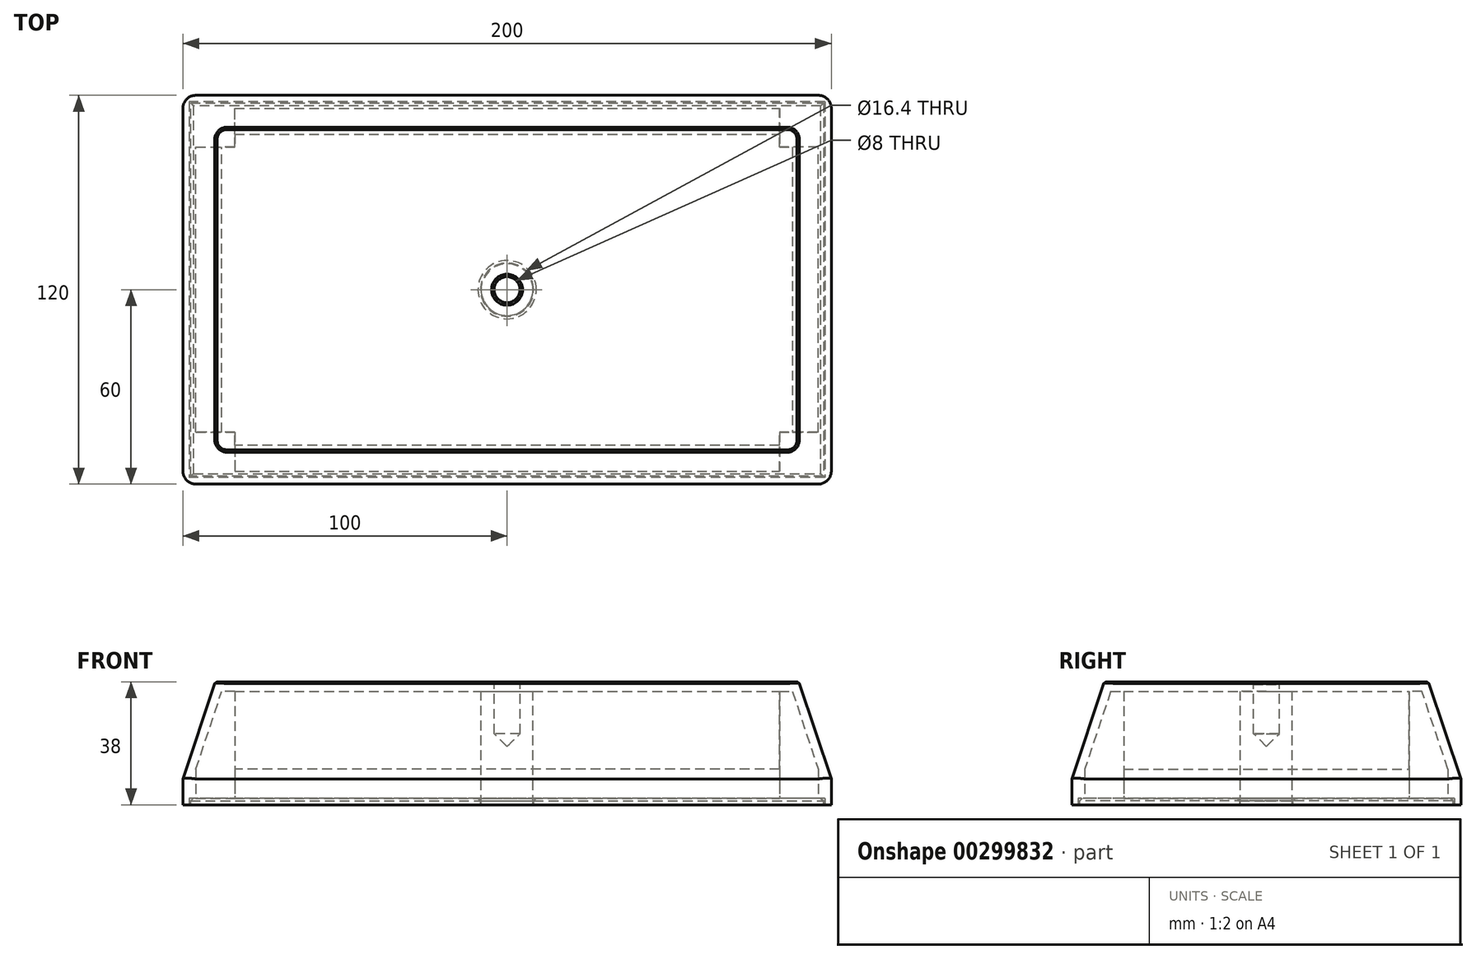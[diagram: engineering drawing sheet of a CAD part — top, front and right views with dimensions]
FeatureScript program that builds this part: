
annotation { "Feature Type Name" : "Feature", "Feature Type Description" : "" }
export const myFeature = defineFeature(function(context is Context, id is Id, definition is map)
    precondition{}
    {
        {
            var Q0;
            Q0=qCreatedBy(makeId("Top.planeOp"),FACE);
            var sketch = newSketch(context, id + "F0", { "sketchPlane" : qUnion([Q0])});
            skLineSegment(sketch, "E0.bottom", {"start": v(100, -60) * mm, "end": v(-100, -60) * mm});
            skLineSegment(sketch, "E0.top", {"start": v(100, 60) * mm, "end": v(-100, 60) * mm});
            skLineSegment(sketch, "E0.left", {"start": v(100, -60) * mm, "end": v(100, 60) * mm});
            skLineSegment(sketch, "E0.right", {"start": v(-100, -60) * mm, "end": v(-100, 60) * mm});
            skPoint(sketch, "E0.middle", {"position": v(0, 0) * mm});
            skSolve(sketch);
        }
        {
            var Q0;
            Q0 = qSketchRegion(id + "F0", true);
            extrude(context, id + "F1", {"entities" : qUnion([Q0]), "depth" : 38 * mm, "offsetDistance" : 25 * mm});
        }
        {
            var Q0;
            Q0=makeQuery(id+"F1.opExtrude","CAP_FACE",FACE,{"disambiguationData":[OSD([sQuery(id+"F0.wireOp",EDGE,"E0.bottom"),sQuery(id+"F0.wireOp",EDGE,"E0.top"),sQuery(id+"F0.wireOp",EDGE,"E0.left"),sQuery(id+"F0.wireOp",EDGE,"E0.right")])],"isStart":true});
            var sketch = newSketch(context, id + "F2", { "sketchPlane" : qUnion([Q0])});
            skLineSegment(sketch, "E1.bottom", {"start": v(84, -56) * mm, "end": v(-84, -56) * mm});
            skLineSegment(sketch, "E1.top", {"start": v(84, 56) * mm, "end": v(-84, 56) * mm});
            skLineSegment(sketch, "E1.left", {"start": v(96, -44) * mm, "end": v(96, 44) * mm});
            skLineSegment(sketch, "E1.right", {"start": v(-96, -44) * mm, "end": v(-96, 44) * mm});
            skPoint(sketch, "E1.middle", {"position": v(0, 0) * mm});
            skLineSegment(sketch, "E2", {"start": v(84, 56) * mm, "end": v(84, 44) * mm});
            skLineSegment(sketch, "E3", {"start": v(84, 44) * mm, "end": v(96, 44) * mm});
            skLineSegment(sketch, "E4.MirrorCS", {"start": v(-84, 56) * mm, "end": v(-84, 44) * mm});
            skLineSegment(sketch, "E5.MirrorCS", {"start": v(-84, 44) * mm, "end": v(-96, 44) * mm});
            skLineSegment(sketch, "E6.MirrorCS", {"start": v(84, -44) * mm, "end": v(96, -44) * mm});
            skLineSegment(sketch, "E7.MirrorCS", {"start": v(84, -56) * mm, "end": v(84, -44) * mm});
            skLineSegment(sketch, "E8.MirrorCS", {"start": v(-84, -56) * mm, "end": v(-84, -44) * mm});
            skLineSegment(sketch, "E9.MirrorCS", {"start": v(-84, -44) * mm, "end": v(-96, -44) * mm});
            skPoint(sketch, "E10.orphan", {"position": v(96, 56) * mm});
            skPoint(sketch, "E11.orphan", {"position": v(96, -56) * mm});
            skPoint(sketch, "E12.orphan", {"position": v(-96, -56) * mm});
            skPoint(sketch, "E13.orphan", {"position": v(-96, 56) * mm});
            skSolve(sketch);
        }
        {
            var Q0;
            Q0 = qSketchRegion(id + "F2", true);
            extrude(context, id + "F3", {"entities" : qUnion([Q0]), "operationType" : NewBodyOperationType.REMOVE, "oppositeDirection" : true, "depth" : 35 * mm, "offsetDistance" : 25 * mm});
        }
        {
            var Q0;
            Q0=makeQuery(id+"F1.opExtrude","CAP_FACE",FACE,{"disambiguationData":[OSD([sQuery(id+"F0.wireOp",EDGE,"E0.bottom"),sQuery(id+"F0.wireOp",EDGE,"E0.top"),sQuery(id+"F0.wireOp",EDGE,"E0.left"),sQuery(id+"F0.wireOp",EDGE,"E0.right")])],"isStart":true});
            var sketch = newSketch(context, id + "F4", { "sketchPlane" : qUnion([Q0])});
            skLineSegment(sketch, "E14.bottom", {"start": v(98, -58) * mm, "end": v(-98, -58) * mm});
            skLineSegment(sketch, "E14.top", {"start": v(98, 58) * mm, "end": v(-98, 58) * mm});
            skLineSegment(sketch, "E14.left", {"start": v(98, -58) * mm, "end": v(98, 58) * mm});
            skLineSegment(sketch, "E14.right", {"start": v(-98, -58) * mm, "end": v(-98, 58) * mm});
            skPoint(sketch, "E14.middle", {"position": v(0, 0) * mm});
            skSolve(sketch);
        }
        {
            var Q0;
            Q0 = qSketchRegion(id + "F4", true);
            extrude(context, id + "F5", {"entities" : qUnion([Q0]), "operationType" : NewBodyOperationType.REMOVE, "oppositeDirection" : true, "depth" : 2 * mm, "offsetDistance" : 25 * mm});
        }
        {
            var Q0;
            Q0=makeQuery(id+"F3.boolean.opBoolean","COPY",FACE,{"derivedFrom":makeQuery(id+"F3.opExtrude","CAP_FACE",FACE,{"disambiguationData":[OSD([sQuery(id+"F2.wireOp",EDGE,"E1.bottom"),sQuery(id+"F2.wireOp",EDGE,"E1.top"),sQuery(id+"F2.wireOp",EDGE,"E1.left"),sQuery(id+"F2.wireOp",EDGE,"E1.right"),sQuery(id+"F2.wireOp",EDGE,"E2"),sQuery(id+"F2.wireOp",EDGE,"E3"),sQuery(id+"F2.wireOp",EDGE,"E4.MirrorCS"),sQuery(id+"F2.wireOp",EDGE,"E5.MirrorCS"),sQuery(id+"F2.wireOp",EDGE,"E6.MirrorCS"),sQuery(id+"F2.wireOp",EDGE,"E7.MirrorCS"),sQuery(id+"F2.wireOp",EDGE,"E8.MirrorCS"),sQuery(id+"F2.wireOp",EDGE,"E9.MirrorCS")])],"isStart":false})});
            var sketch = newSketch(context, id + "F6", { "sketchPlane" : qUnion([Q0])});
            skCircle(sketch, "E15", {"center": v(0, 0) * mm, "radius": 8 * mm});
            skSolve(sketch);
        }
        {
            var Q0;
            Q0 = qSketchRegion(id + "F6", true);
            var Q1;
            Q1=makeQuery(id+"F1.opExtrude","CAP_FACE",FACE,{"disambiguationData":[OSD([sQuery(id+"F0.wireOp",EDGE,"E0.bottom"),sQuery(id+"F0.wireOp",EDGE,"E0.top"),sQuery(id+"F0.wireOp",EDGE,"E0.left"),sQuery(id+"F0.wireOp",EDGE,"E0.right")])],"isStart":true});
            extrude(context, id + "F7", {"entities" : qUnion([Q0]), "operationType" : NewBodyOperationType.ADD, "endBound" : BoundingType.UP_TO_SURFACE, "depth" : 28 * mm, "endBoundEntityFace" : qUnion([Q1]), "offsetDistance" : 25 * mm});
        }
        {
            var Q0;
            Q0=makeQuery(id+"F3.boolean.opBoolean","COPY",EDGE,{"derivedFrom":makeQuery(id+"F3.opExtrude","CAP_EDGE",EDGE,{"disambiguationData":[OSD([sQuery(id+"F2.wireOp",EDGE,"E1.top")])],"isStart":false})});
            var Q1;
            Q1=makeQuery(id+"F3.boolean.opBoolean","COPY",EDGE,{"derivedFrom":makeQuery(id+"F3.opExtrude","CAP_EDGE",EDGE,{"disambiguationData":[OSD([sQuery(id+"F2.wireOp",EDGE,"E1.left")])],"isStart":false})});
            var Q2;
            Q2=makeQuery(id+"F3.boolean.opBoolean","COPY",EDGE,{"derivedFrom":makeQuery(id+"F3.opExtrude","CAP_EDGE",EDGE,{"disambiguationData":[OSD([sQuery(id+"F2.wireOp",EDGE,"E1.bottom")])],"isStart":false})});
            var Q3;
            Q3=makeQuery(id+"F3.boolean.opBoolean","COPY",EDGE,{"derivedFrom":makeQuery(id+"F3.opExtrude","CAP_EDGE",EDGE,{"disambiguationData":[OSD([sQuery(id+"F2.wireOp",EDGE,"E1.right")])],"isStart":false})});
            var Q4;
            Q4=makeQuery(id+"F7.opExtrude","CAP_EDGE",EDGE,{"disambiguationData":[OSD([sQuery(id+"F6.wireOp",EDGE,"E15")])],"isStart":true});
            chamfer(context, id + "F8", {"entities" : qUnion([Q0, Q1, Q2, Q3, Q4]), "chamferType" : ChamferType.TWO_OFFSETS, "width1" : 8 * mm, "oppositeDirection" : false, "width2" : 24 * mm, "tangentPropagation" : true});
        }
        {
            var Q0;
            Q0=makeQuery(id+"F1.opExtrude","CAP_FACE",FACE,{"disambiguationData":[OSD([sQuery(id+"F0.wireOp",EDGE,"E0.bottom"),sQuery(id+"F0.wireOp",EDGE,"E0.top"),sQuery(id+"F0.wireOp",EDGE,"E0.left"),sQuery(id+"F0.wireOp",EDGE,"E0.right")])],"isStart":false});
            chamfer(context, id + "F9", {"entities" : qUnion([Q0]), "chamferType" : ChamferType.TWO_OFFSETS, "width1" : 30 * mm, "oppositeDirection" : false, "width2" : 10 * mm, "tangentPropagation" : true});
        }
        {
            var Q0;
            Q0=makeQuery(id+"F9.opChamfer","BLEND_EDGE",EDGE,{"blendedFrom":[makeQuery(id+"F1.opExtrude","CAP_EDGE",EDGE,{"disambiguationData":[OSD([sQuery(id+"F0.wireOp",EDGE,"E0.bottom")])],"isStart":false}),makeQuery(id+"F1.opExtrude","CAP_EDGE",EDGE,{"disambiguationData":[OSD([sQuery(id+"F0.wireOp",EDGE,"E0.left")])],"isStart":false})],"blendedInto":[]});
            var Q1;
            Q1=makeQuery(id+"F9.opChamfer","BLEND_EDGE",EDGE,{"blendedFrom":[makeQuery(id+"F1.opExtrude","CAP_EDGE",EDGE,{"disambiguationData":[OSD([sQuery(id+"F0.wireOp",EDGE,"E0.top")])],"isStart":false}),makeQuery(id+"F1.opExtrude","CAP_EDGE",EDGE,{"disambiguationData":[OSD([sQuery(id+"F0.wireOp",EDGE,"E0.left")])],"isStart":false})],"blendedInto":[]});
            var Q2;
            Q2=makeQuery(id+"F9.opChamfer","BLEND_EDGE",EDGE,{"blendedFrom":[makeQuery(id+"F1.opExtrude","CAP_EDGE",EDGE,{"disambiguationData":[OSD([sQuery(id+"F0.wireOp",EDGE,"E0.top")])],"isStart":false}),makeQuery(id+"F1.opExtrude","CAP_EDGE",EDGE,{"disambiguationData":[OSD([sQuery(id+"F0.wireOp",EDGE,"E0.right")])],"isStart":false})],"blendedInto":[]});
            var Q3;
            Q3=makeQuery(id+"F9.opChamfer","BLEND_EDGE",EDGE,{"blendedFrom":[makeQuery(id+"F1.opExtrude","CAP_EDGE",EDGE,{"disambiguationData":[OSD([sQuery(id+"F0.wireOp",EDGE,"E0.bottom")])],"isStart":false}),makeQuery(id+"F1.opExtrude","CAP_EDGE",EDGE,{"disambiguationData":[OSD([sQuery(id+"F0.wireOp",EDGE,"E0.right")])],"isStart":false})],"blendedInto":[]});
            var Q4;
            Q4=makeQuery(id+"F1.opExtrude","SWEPT_EDGE",EDGE,{"disambiguationData":[OSD([sQuery(id+"F0.wireOp",EDGE,"E0.bottom"),sQuery(id+"F0.wireOp",EDGE,"E0.left")])]});
            var Q5;
            Q5=makeQuery(id+"F1.opExtrude","SWEPT_EDGE",EDGE,{"disambiguationData":[OSD([sQuery(id+"F0.wireOp",EDGE,"E0.top"),sQuery(id+"F0.wireOp",EDGE,"E0.left")])]});
            var Q6;
            Q6=makeQuery(id+"F1.opExtrude","SWEPT_EDGE",EDGE,{"disambiguationData":[OSD([sQuery(id+"F0.wireOp",EDGE,"E0.top"),sQuery(id+"F0.wireOp",EDGE,"E0.right")])]});
            var Q7;
            Q7=makeQuery(id+"F1.opExtrude","SWEPT_EDGE",EDGE,{"disambiguationData":[OSD([sQuery(id+"F0.wireOp",EDGE,"E0.bottom"),sQuery(id+"F0.wireOp",EDGE,"E0.right")])]});
            fillet(context, id + "F10", {"entities" : qUnion([Q0, Q1, Q2, Q3, Q4, Q5, Q6, Q7]), "tangentPropagation" : true, "radius" : 4 * mm, "defaultsChanged" : true, "vertexSettings" : [], "allowEdgeOverflow" : false});
        }
        {
            var Q0;
            Q0=makeQuery(id+"F1.opExtrude","CAP_FACE",FACE,{"disambiguationData":[OSD([sQuery(id+"F0.wireOp",EDGE,"E0.bottom"),sQuery(id+"F0.wireOp",EDGE,"E0.top"),sQuery(id+"F0.wireOp",EDGE,"E0.left"),sQuery(id+"F0.wireOp",EDGE,"E0.right")])],"isStart":false});
            var sketch = newSketch(context, id + "F11", { "sketchPlane" : qUnion([Q0])});
            skCircle(sketch, "E16", {"center": v(0, 0) * mm, "radius": 4 * mm});
            skSolve(sketch);
        }
        {
            var Q0;
            Q0 = qSketchRegion(id + "F11", true);
            extrude(context, id + "F12", {"entities" : qUnion([Q0]), "operationType" : NewBodyOperationType.REMOVE, "oppositeDirection" : true, "depth" : 20 * mm, "offsetDistance" : 25 * mm});
        }
        {
            var Q0;
            Q0=makeQuery(id+"F12.boolean.opBoolean","COPY",EDGE,{"derivedFrom":makeQuery(id+"F12.opExtrude","CAP_EDGE",EDGE,{"disambiguationData":[OSD([sQuery(id+"F11.wireOp",EDGE,"E16")])],"isStart":false})});
            chamfer(context, id + "F13", {"entities" : qUnion([Q0]), "width" : 4 * mm, "tangentPropagation" : true});
        }
        {
            var Q0;
            Q0=makeQuery(id+"F12.boolean.opBoolean","COPY",EDGE,{"derivedFrom":makeQuery(id+"F12.opExtrude","CAP_EDGE",EDGE,{"disambiguationData":[OSD([sQuery(id+"F11.wireOp",EDGE,"E16")])],"isStart":true})});
            var Q1;
            Q1=makeQuery(id+"F1.opExtrude","CAP_FACE",FACE,{"disambiguationData":[OSD([sQuery(id+"F0.wireOp",EDGE,"E0.bottom"),sQuery(id+"F0.wireOp",EDGE,"E0.top"),sQuery(id+"F0.wireOp",EDGE,"E0.left"),sQuery(id+"F0.wireOp",EDGE,"E0.right")])],"isStart":false});
            chamfer(context, id + "F14", {"entities" : qUnion([Q0, Q1]), "width" : 0.8 * mm, "tangentPropagation" : true});
        }
        {
            var Q0;
            Q0=makeQuery(id+"F5.boolean.opBoolean","COPY",FACE,{"derivedFrom":makeQuery(id+"F5.opExtrude","CAP_FACE",FACE,{"disambiguationData":[OSD([sQuery(id+"F4.wireOp",EDGE,"E14.bottom"),sQuery(id+"F4.wireOp",EDGE,"E14.top"),sQuery(id+"F4.wireOp",EDGE,"E14.left"),sQuery(id+"F4.wireOp",EDGE,"E14.right")])],"isStart":false})});
            var sketch = newSketch(context, id + "F15", { "sketchPlane" : qUnion([Q0])});
            skLineSegment(sketch, "E17.bottom", {"start": v(97.6, -57.6) * mm, "end": v(-97.6, -57.6) * mm});
            skLineSegment(sketch, "E17.top", {"start": v(97.6, 57.6) * mm, "end": v(-97.6, 57.6) * mm});
            skLineSegment(sketch, "E17.left", {"start": v(97.6, -57.6) * mm, "end": v(97.6, 57.6) * mm});
            skLineSegment(sketch, "E17.right", {"start": v(-97.6, -57.6) * mm, "end": v(-97.6, 57.6) * mm});
            skPoint(sketch, "E17.middle", {"position": v(0, 0) * mm});
            skCircle(sketch, "E18", {"center": v(0, 0) * mm, "radius": 8.2 * mm});
            skSolve(sketch);
        }
        {
            var Q0;
            Q0 = qSketchRegion(id + "F15", true);
            extrude(context, id + "F16", {"entities" : qUnion([Q0]), "depth" : 2 * mm, "offsetDistance" : 25 * mm});
        }
        {
            var Q0;
            Q0=makeQuery(id+"F16.opExtrude","CAP_FACE",FACE,{"disambiguationData":[OSD([sQuery(id+"F15.wireOp",EDGE,"E17.bottom"),sQuery(id+"F15.wireOp",EDGE,"E17.top"),sQuery(id+"F15.wireOp",EDGE,"E17.left"),sQuery(id+"F15.wireOp",EDGE,"E17.right"),sQuery(id+"F15.wireOp",EDGE,"E18")])],"isStart":true});
            chamfer(context, id + "F17", {"entities" : qUnion([Q0]), "width" : 0.8 * mm, "tangentPropagation" : true});
        }
    });
